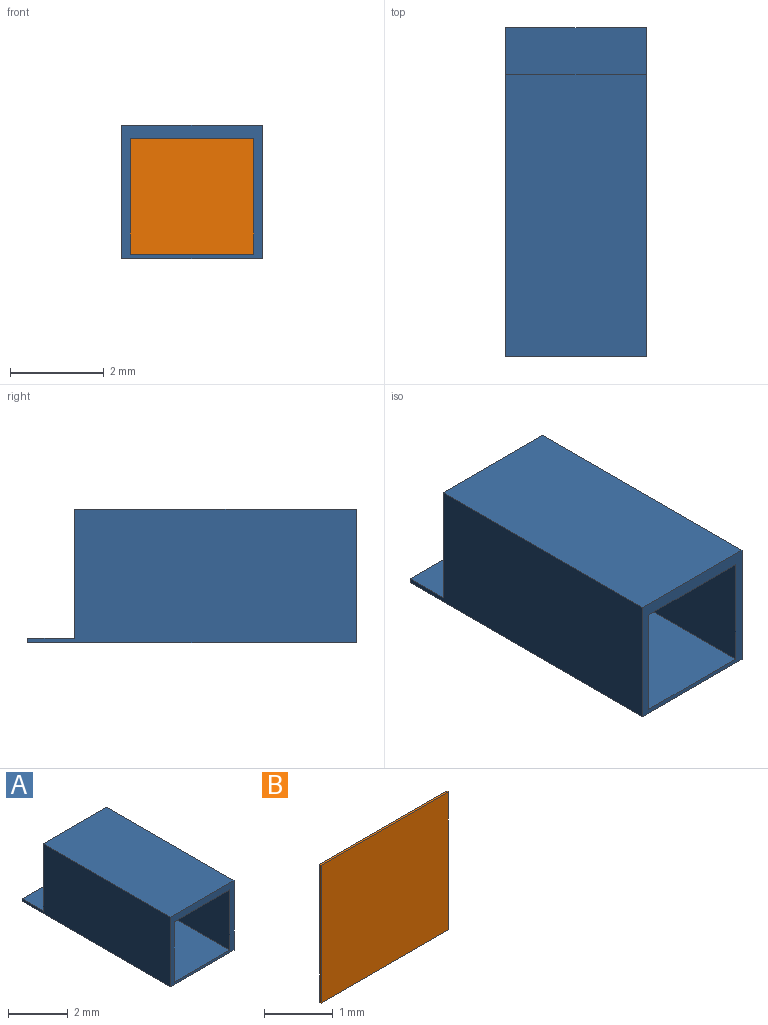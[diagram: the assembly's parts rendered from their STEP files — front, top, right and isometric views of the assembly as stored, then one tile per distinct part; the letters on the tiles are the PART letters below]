
ASSEMBLY  parts=2 mates=1
PART A: 11 faces, bbox 3x7x2.8 mm
  f0: plane 7x2.85mm, normal (-1,0,0), area 17.2mm2, adj f5,f6,f7,f8,f9,f10
  f1: plane 6x2.46mm, normal (1,0,0), area 14.8mm2, adj f2,f6,f7,f8
  f2: plane 6x2.62mm, normal (0,0,-1), area 15.7mm2, adj f1,f3,f6,f7
  f3: plane 6x2.46mm, normal (-1,0,0), area 14.8mm2, adj f2,f6,f7,f8
  f4: plane 7x2.85mm, normal (1,0,0), area 17.2mm2, adj f5,f6,f7,f8,f9,f10
  f5: plane 6x3mm, normal (0,0,1), area 18mm2, adj f0,f4,f6,f7
  f6: plane 3x2.85mm, normal (0,-1,0), area 2.1mm2, adj f0,f1,f2,f3,f4,f5,f8,f10
  f7: plane 3x2.75mm, normal (0,1,0), area 1.8mm2, adj f0,f1,f2,f3,f4,f5,f8
  f8: plane 7x3mm, normal (0,0,1), area 18.7mm2, adj f0,f1,f3,f4,f6,f7,f9
  f9: plane 3x0.1mm, normal (0,1,0), area 0.3mm2, adj f0,f4,f8,f10
  f10: plane 7x3mm, normal (0,0,-1), area 21mm2, adj f0,f4,f6,f9
PART B: 6 faces, bbox 2.6x0x2.5 mm
  f0: plane 2.46x0.03mm, normal (-1,0,0), area 0.1mm2, adj f1,f3,f4,f5
  f1: plane 2.62x0.03mm, normal (0,0,-1), area 0.1mm2, adj f0,f2,f4,f5
  f2: plane 2.46x0.03mm, normal (1,0,0), area 0.1mm2, adj f1,f3,f4,f5
  f3: plane 2.62x0.03mm, normal (0,0,1), area 0.1mm2, adj f0,f2,f4,f5
  f4: plane 2.62x2.46mm, normal (0,-1,0), area 6.4mm2, adj f0,f1,f2,f3
  f5: plane 2.62x2.46mm, normal (0,1,0), area 6.4mm2, adj f0,f1,f2,f3
PLACE A t=(0.83,2.68,-0.85)mm
PLACE B t=(0.83,2.6,-0.85)mm
MATE parallel B.f5 <-> A.f7  axis (0,1,0) through (2.14,2.58,1.61)mm
